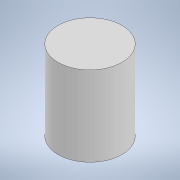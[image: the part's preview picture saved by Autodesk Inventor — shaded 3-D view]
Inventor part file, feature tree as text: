
AUTODESK INVENTOR PART (.ipt)
format: ipt  version: 2021 (Build 250183000, 183)  size: 87,040 bytes
history: native  units: mm
features: extrude x1, sketch x1
ambient origin geometry x8: Origin, YZ Plane, XZ Plane, XY Plane, X Axis, Y Axis, Z Axis, Center Point
bodies: Solid1 (feature_tree)
feature tree (2):
  extrude  "Extrusion1"  Depth=10.0mm TaperAngle=0.0deg
  sketch  "Sketch1"  dims[d0=8.0mm d1=10.0mm d2=0.0mm]
